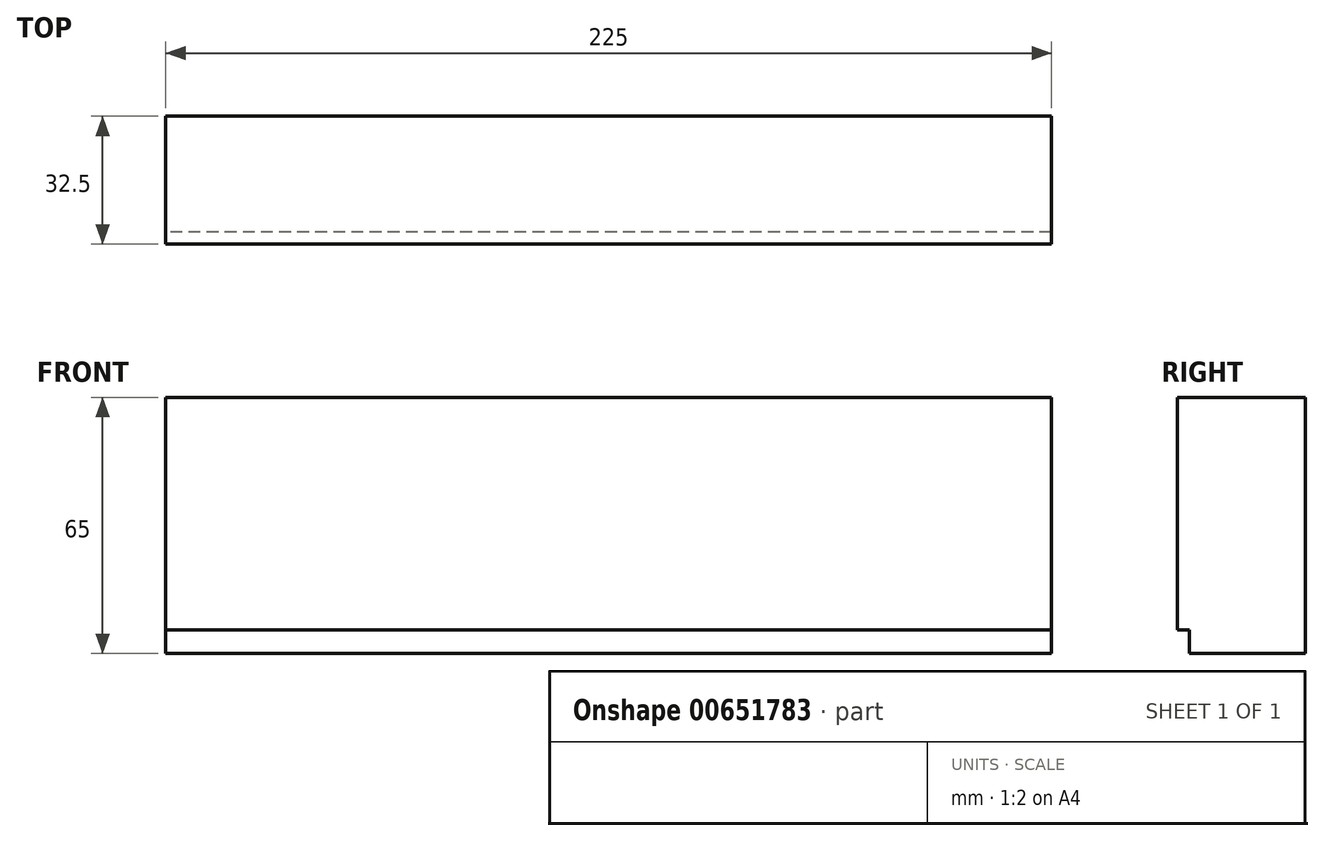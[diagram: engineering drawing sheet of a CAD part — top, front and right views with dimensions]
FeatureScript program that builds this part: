
annotation { "Feature Type Name" : "Feature", "Feature Type Description" : "" }
export const myFeature = defineFeature(function(context is Context, id is Id, definition is map)
    precondition{}
    {
        {
            var Q0;
            Q0=qCreatedBy(makeId("Right.planeOp"),FACE);
            var sketch = newSketch(context, id + "F0", { "sketchPlane" : qUnion([Q0])});
            skLineSegment(sketch, "E0.bottom", {"start": v(3, 0) * mm, "end": v(32.5, 0) * mm});
            skLineSegment(sketch, "E0.top", {"start": v(0, 65) * mm, "end": v(32.5, 65) * mm});
            skLineSegment(sketch, "E0.left", {"start": v(0, 6) * mm, "end": v(0, 65) * mm});
            skLineSegment(sketch, "E0.right", {"start": v(32.5, 0) * mm, "end": v(32.5, 65) * mm});
            skLineSegment(sketch, "E1", {"start": v(3, 0) * mm, "end": v(3, 6) * mm});
            skLineSegment(sketch, "E2", {"start": v(3, 6) * mm, "end": v(0, 6) * mm});
            skPoint(sketch, "E3", {"position": v(0, 29) * mm});
            skPoint(sketch, "E4.orphan", {"position": v(0, 0) * mm});
            skSolve(sketch);
        }
        {
            var Q0;
            Q0 = qSketchRegion(id + "F0", true);
            extrude(context, id + "F1", {"entities" : qUnion([Q0]), "depth" : 225 * mm, "offsetDistance" : 25 * mm});
        }
    });
